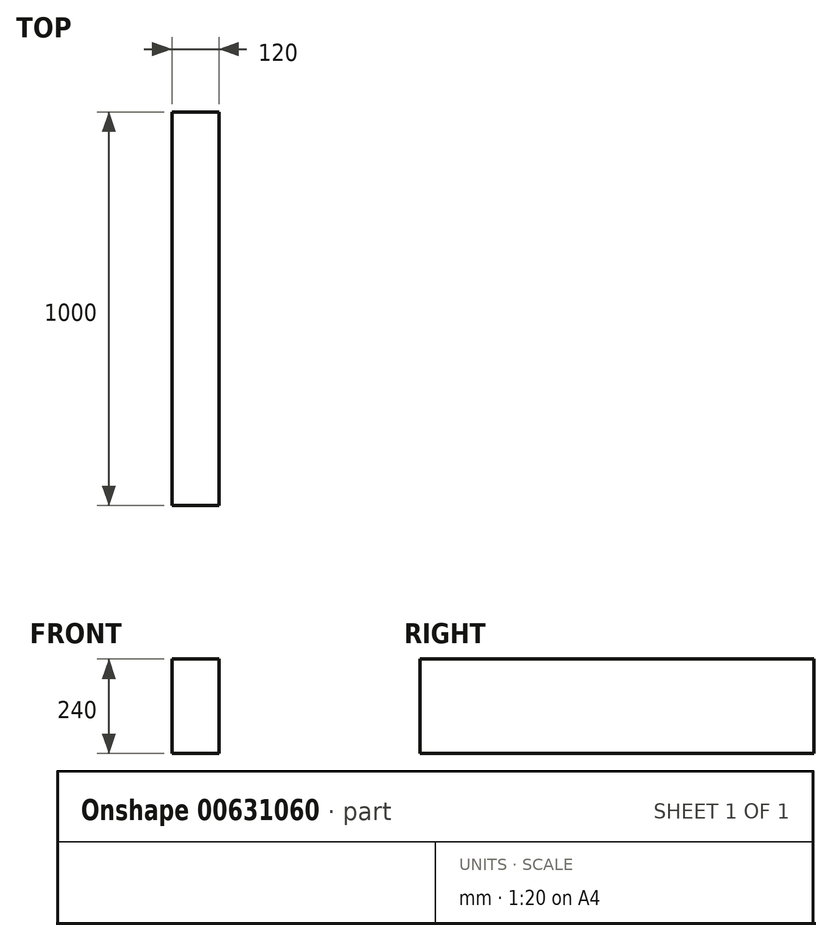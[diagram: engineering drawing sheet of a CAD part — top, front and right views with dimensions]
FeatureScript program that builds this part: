
annotation { "Feature Type Name" : "Feature", "Feature Type Description" : "" }
export const myFeature = defineFeature(function(context is Context, id is Id, definition is map)
    precondition{}
    {
        {
            var Q0;
            Q0=qCreatedBy(makeId("Front.planeOp"),FACE);
            var sketch = newSketch(context, id + "F0", { "sketchPlane" : qUnion([Q0])});
            skLineSegment(sketch, "E0.bottom", {"start": v(-18.48, 231.1) * mm, "end": v(101.52, 231.1) * mm});
            skLineSegment(sketch, "E0.top", {"start": v(-18.48, -8.9) * mm, "end": v(101.52, -8.9) * mm});
            skLineSegment(sketch, "E0.left", {"start": v(-18.48, 231.1) * mm, "end": v(-18.48, -8.9) * mm});
            skLineSegment(sketch, "E0.right", {"start": v(101.52, 231.1) * mm, "end": v(101.52, -8.9) * mm});
            skSolve(sketch);
        }
        {
            var Q0;
            Q0=makeQuery(id+"F0.imprint","IMPRINT",FACE,{"disambiguationData":[TD([[makeQuery(id+"F0.imprint","IMPRINT",EDGE,{"derivedFrom":sQuery(id+"F0.wireOp",EDGE,"E0.bottom")}),-1.0]])]});
            var Q1;
            Q1=qSketchRegion(id+"F0",true);
            extrude(context, id + "F1", {"entities" : qUnion([Q0, Q1]), "depth" : 1000 * mm, "offsetDistance" : 25 * mm});
        }
    });
